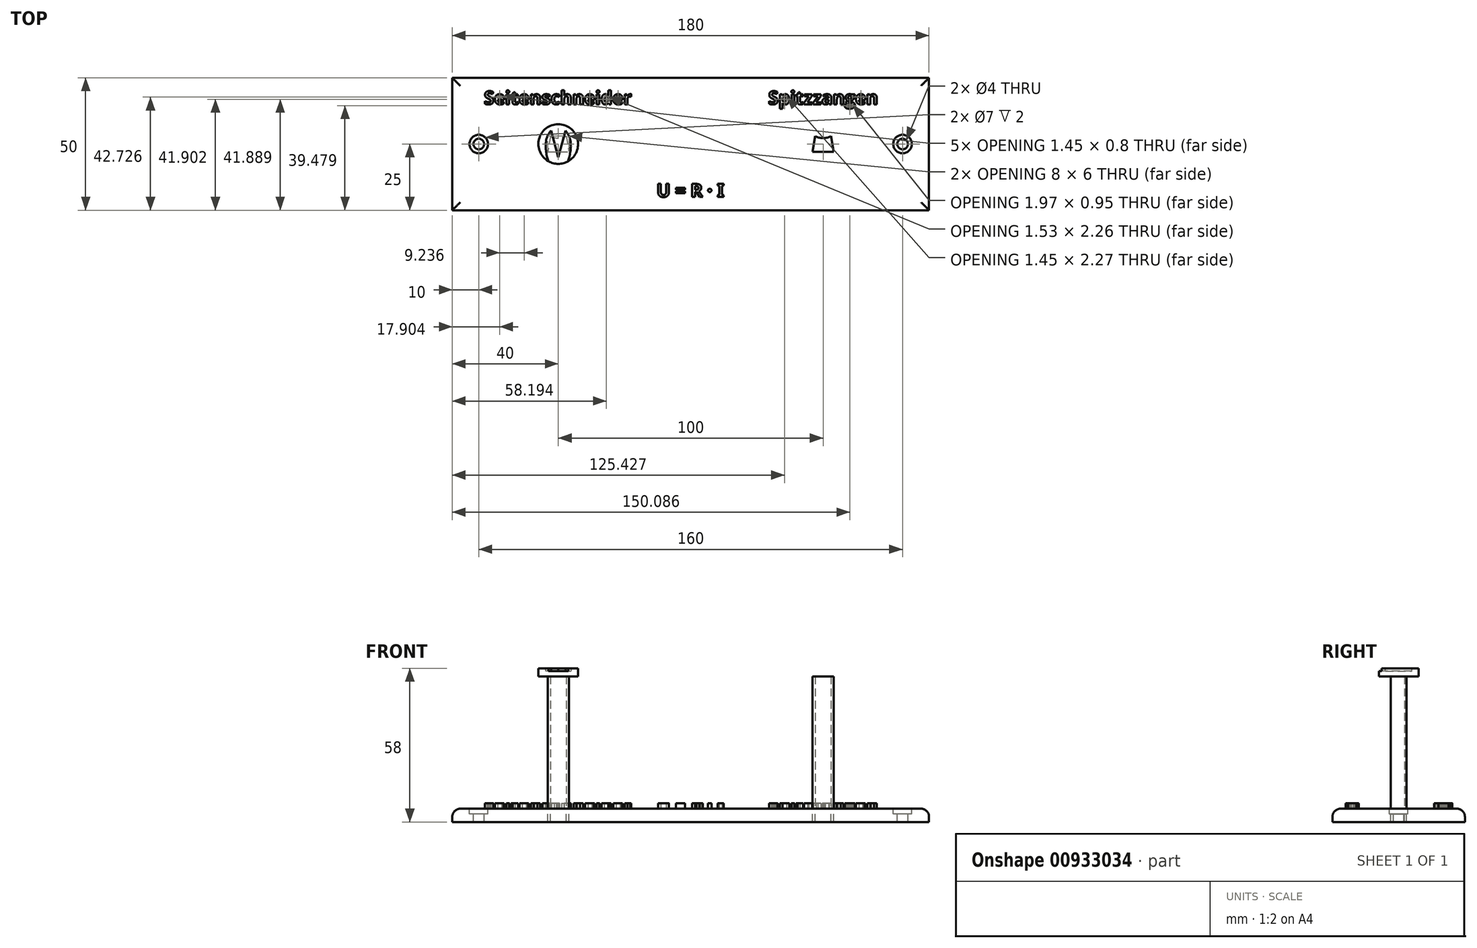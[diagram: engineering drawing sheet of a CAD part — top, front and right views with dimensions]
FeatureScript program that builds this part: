
annotation { "Feature Type Name" : "Feature", "Feature Type Description" : "" }
export const myFeature = defineFeature(function(context is Context, id is Id, definition is map)
    precondition{}
    {
        {
            var Q0;
            Q0=qCreatedBy(makeId("Top.planeOp"),FACE);
            var sketch = newSketch(context, id + "F0", { "sketchPlane" : qUnion([Q0])});
            skLineSegment(sketch, "E0.bottom", {"start": v(-90, 25) * mm, "end": v(90, 25) * mm});
            skLineSegment(sketch, "E0.top", {"start": v(-90, -25) * mm, "end": v(90, -25) * mm});
            skLineSegment(sketch, "E0.left", {"start": v(-90, 25) * mm, "end": v(-90, -25) * mm});
            skLineSegment(sketch, "E0.right", {"start": v(90, 25) * mm, "end": v(90, -25) * mm});
            skPoint(sketch, "E0.middle", {"position": v(0, 0) * mm});
            skPoint(sketch, "E1", {"position": v(-50, 0) * mm});
            skLineSegment(sketch, "E2", {"start": v(0, 25) * mm, "end": v(0, -25) * mm, "construction": true});
            skLineSegment(sketch, "E3", {"start": v(-90, 0) * mm, "end": v(0, 0) * mm, "construction": true});
            skLineSegment(sketch, "E4", {"start": v(0, 0) * mm, "end": v(90, 0) * mm, "construction": true});
            skPoint(sketch, "E5", {"position": v(50, 0) * mm});
            skLineSegment(sketch, "E6", {"start": v(-50, 25) * mm, "end": v(-50, -25) * mm, "construction": true});
            skArc(sketch, "E7", {"start": v(-53, 3) * mm, "mid": v(-51.55, 2.44) * mm, "end": v(-50, 2.25) * mm});
            skLineSegment(sketch, "E8", {"start": v(-53, 3) * mm, "end": v(-53.5, 0) * mm});
            skLineSegment(sketch, "E9", {"start": v(-53.5, 0) * mm, "end": v(-54, -3) * mm});
            skLineSegment(sketch, "E10", {"start": v(-54, -3) * mm, "end": v(-50, -3) * mm});
            skLineSegment(sketch, "E11.MirrorCS", {"start": v(-46, -3) * mm, "end": v(-50, -3) * mm});
            skLineSegment(sketch, "E12.MirrorCS", {"start": v(-47, 3) * mm, "end": v(-46.5, 0) * mm});
            skLineSegment(sketch, "E13.MirrorCS", {"start": v(-46.5, 0) * mm, "end": v(-46, -3) * mm});
            skArc(sketch, "E14.MirrorCS", {"start": v(-47, 3) * mm, "mid": v(-48.45, 2.44) * mm, "end": v(-50, 2.25) * mm});
            skLineSegment(sketch, "E15.MirrorCS", {"start": v(47, 3) * mm, "end": v(46.5, 0) * mm});
            skLineSegment(sketch, "E16.MirrorCS", {"start": v(46.5, 0) * mm, "end": v(46, -3) * mm});
            skLineSegment(sketch, "E17.MirrorCS", {"start": v(54, -3) * mm, "end": v(50, -3) * mm});
            skLineSegment(sketch, "E18.MirrorCS", {"start": v(46, -3) * mm, "end": v(50, -3) * mm});
            skLineSegment(sketch, "E19.MirrorCS", {"start": v(53, 3) * mm, "end": v(53.5, 0) * mm});
            skLineSegment(sketch, "E20.MirrorCS", {"start": v(53.5, 0) * mm, "end": v(54, -3) * mm});
            skArc(sketch, "E21.MirrorCS", {"start": v(53, 3) * mm, "mid": v(51.55, 2.44) * mm, "end": v(50, 2.25) * mm});
            skArc(sketch, "E22.MirrorCS", {"start": v(47, 3) * mm, "mid": v(48.45, 2.44) * mm, "end": v(50, 2.25) * mm});
            skText(sketch, "E23", { "text": "Seitenschneider", "fontName": "OpenSans-Bold.ttf"});
            skText(sketch, "E24", { "text": "Spitzzangen", "fontName": "OpenSans-Bold.ttf"});
            skLineSegment(sketch, "E25", {"start": v(50, 25) * mm, "end": v(50, -25) * mm, "construction": true});
            skText(sketch, "E26", { "text": "U = R   I", "fontName": "NotoSans-Bold.ttf"});
            skCircle(sketch, "E27", {"center": v(7.2, -17.5) * mm, "radius": 0.65 * mm});
            skPoint(sketch, "E27.centerSnap0", {"position": v(0, -17.5) * mm});
            skPoint(sketch, "E28", {"position": v(-80, 0) * mm});
            skPoint(sketch, "E29.MirrorP", {"position": v(80, 0) * mm});
            const initialGuessF0  = {"E23": [-0.07803, 0.015, 1, 0, 0.005], "E24": [0.0293, 0.015, 1, 0, 0.005], "E26": [-0.01288, -0.02, 1, 0, 0.005]};
            skSetInitialGuess(sketch, initialGuessF0);
            skSolve(sketch);
        }
        {
            var Q0;
            Q0=makeQuery(id+"F0.imprint","IMPRINT",FACE,{"disambiguationData":[TD([[makeQuery(id+"F0.imprint","IMPRINT",EDGE,{"derivedFrom":sQuery(id+"F0.wireOp",EDGE,"E0.bottom")}),-1.0]])]});
            var Q1;
            Q1=makeQuery(id+"F0.imprint","IMPRINT",FACE,{"disambiguationData":[TD([[makeQuery(id+"F0.imprint","IMPRINT",EDGE,{"derivedFrom":sQuery(id+"F0.wireOp",EDGE,"E23.sketch_text.stroke-211")}),-1.0]])]});
            var Q2;
            Q2=makeQuery(id+"F0.imprint","IMPRINT",FACE,{"disambiguationData":[TD([[makeQuery(id+"F0.imprint","IMPRINT",EDGE,{"derivedFrom":sQuery(id+"F0.wireOp",EDGE,"E24.sketch_text.stroke-51")}),-1.0]])]});
            var Q3;
            Q3=makeQuery(id+"F0.imprint","IMPRINT",FACE,{"disambiguationData":[TD([[makeQuery(id+"F0.imprint","IMPRINT",EDGE,{"derivedFrom":sQuery(id+"F0.wireOp",EDGE,"E24.sketch_text.stroke-78")}),-1.0]])]});
            var Q4;
            Q4=makeQuery(id+"F0.imprint","IMPRINT",FACE,{"disambiguationData":[TD([[makeQuery(id+"F0.imprint","IMPRINT",EDGE,{"derivedFrom":sQuery(id+"F0.wireOp",EDGE,"E7")}),-1.0]])]});
            var Q5;
            Q5=makeQuery(id+"F0.imprint","IMPRINT",FACE,{"disambiguationData":[TD([[makeQuery(id+"F0.imprint","IMPRINT",EDGE,{"derivedFrom":sQuery(id+"F0.wireOp",EDGE,"E24.sketch_text.stroke-204")}),-1.0]])]});
            var Q6;
            Q6=makeQuery(id+"F0.imprint","IMPRINT",FACE,{"disambiguationData":[TD([[makeQuery(id+"F0.imprint","IMPRINT",EDGE,{"derivedFrom":sQuery(id+"F0.wireOp",EDGE,"E23.sketch_text.stroke-75")}),-1.0]])]});
            var Q7;
            Q7=makeQuery(id+"F0.imprint","IMPRINT",FACE,{"disambiguationData":[TD([[makeQuery(id+"F0.imprint","IMPRINT",EDGE,{"derivedFrom":sQuery(id+"F0.wireOp",EDGE,"E26.sketch_text.stroke-15")}),-1.0]])]});
            var Q8;
            Q8=makeQuery(id+"F0.imprint","IMPRINT",FACE,{"disambiguationData":[TD([[makeQuery(id+"F0.imprint","IMPRINT",EDGE,{"derivedFrom":sQuery(id+"F0.wireOp",EDGE,"E23.sketch_text.stroke-57")}),-1.0]])]});
            var Q9;
            Q9=makeQuery(id+"F0.imprint","IMPRINT",FACE,{"disambiguationData":[TD([[makeQuery(id+"F0.imprint","IMPRINT",EDGE,{"derivedFrom":sQuery(id+"F0.wireOp",EDGE,"E23.sketch_text.stroke-229")}),1.0]])]});
            var Q10;
            Q10=makeQuery(id+"F0.imprint","IMPRINT",FACE,{"disambiguationData":[TD([[makeQuery(id+"F0.imprint","IMPRINT",EDGE,{"derivedFrom":sQuery(id+"F0.wireOp",EDGE,"E23.sketch_text.stroke-169")}),-1.0]])]});
            var Q11;
            Q11=makeQuery(id+"F0.imprint","IMPRINT",FACE,{"disambiguationData":[TD([[makeQuery(id+"F0.imprint","IMPRINT",EDGE,{"derivedFrom":sQuery(id+"F0.wireOp",EDGE,"E26.sketch_text.stroke-42")}),-1.0]])]});
            var Q12;
            Q12=makeQuery(id+"F0.imprint","IMPRINT",FACE,{"disambiguationData":[TD([[makeQuery(id+"F0.imprint","IMPRINT",EDGE,{"derivedFrom":sQuery(id+"F0.wireOp",EDGE,"E23.sketch_text.stroke-238")}),-1.0]])]});
            var Q13;
            Q13=makeQuery(id+"F0.imprint","IMPRINT",FACE,{"disambiguationData":[TD([[makeQuery(id+"F0.imprint","IMPRINT",EDGE,{"derivedFrom":sQuery(id+"F0.wireOp",EDGE,"E23.sketch_text.stroke-0")}),-1.0]])]});
            var Q14;
            Q14=makeQuery(id+"F0.imprint","IMPRINT",FACE,{"disambiguationData":[TD([[makeQuery(id+"F0.imprint","IMPRINT",EDGE,{"derivedFrom":sQuery(id+"F0.wireOp",EDGE,"E23.sketch_text.stroke-215")}),-1.0]])]});
            var Q15;
            Q15=makeQuery(id+"F0.imprint","IMPRINT",FACE,{"disambiguationData":[TD([[makeQuery(id+"F0.imprint","IMPRINT",EDGE,{"derivedFrom":sQuery(id+"F0.wireOp",EDGE,"E26.sketch_text.stroke-0")}),-1.0]])]});
            var Q16;
            Q16=makeQuery(id+"F0.imprint","IMPRINT",FACE,{"disambiguationData":[TD([[makeQuery(id+"F0.imprint","IMPRINT",EDGE,{"derivedFrom":sQuery(id+"F0.wireOp",EDGE,"E24.sketch_text.stroke-140")}),-1.0]])]});
            var Q17;
            Q17=makeQuery(id+"F0.imprint","IMPRINT",FACE,{"disambiguationData":[TD([[makeQuery(id+"F0.imprint","IMPRINT",EDGE,{"derivedFrom":sQuery(id+"F0.wireOp",EDGE,"E24.sketch_text.stroke-123")}),-1.0]])]});
            var Q18;
            Q18=makeQuery(id+"F0.imprint","IMPRINT",FACE,{"disambiguationData":[TD([[makeQuery(id+"F0.imprint","IMPRINT",EDGE,{"derivedFrom":sQuery(id+"F0.wireOp",EDGE,"E23.sketch_text.stroke-138")}),-1.0]])]});
            var Q19;
            Q19=makeQuery(id+"F0.imprint","IMPRINT",FACE,{"disambiguationData":[TD([[makeQuery(id+"F0.imprint","IMPRINT",EDGE,{"derivedFrom":sQuery(id+"F0.wireOp",EDGE,"E24.sketch_text.stroke-60")}),-1.0]])]});
            var Q20;
            Q20=makeQuery(id+"F0.imprint","IMPRINT",FACE,{"disambiguationData":[TD([[makeQuery(id+"F0.imprint","IMPRINT",EDGE,{"derivedFrom":sQuery(id+"F0.wireOp",EDGE,"E24.sketch_text.stroke-0")}),-1.0]])]});
            var Q21;
            Q21=makeQuery(id+"F0.imprint","IMPRINT",FACE,{"disambiguationData":[TD([[makeQuery(id+"F0.imprint","IMPRINT",EDGE,{"derivedFrom":sQuery(id+"F0.wireOp",EDGE,"E23.sketch_text.stroke-95")}),-1.0]])]});
            var Q22;
            Q22=makeQuery(id+"F0.imprint","IMPRINT",FACE,{"disambiguationData":[TD([[makeQuery(id+"F0.imprint","IMPRINT",EDGE,{"derivedFrom":sQuery(id+"F0.wireOp",EDGE,"E23.sketch_text.stroke-28")}),-1.0]])]});
            var Q23;
            Q23=makeQuery(id+"F0.imprint","IMPRINT",FACE,{"disambiguationData":[TD([[makeQuery(id+"F0.imprint","IMPRINT",EDGE,{"derivedFrom":sQuery(id+"F0.wireOp",EDGE,"E23.sketch_text.stroke-152")}),-1.0]])]});
            var Q24;
            Q24=makeQuery(id+"F0.imprint","IMPRINT",FACE,{"disambiguationData":[TD([[makeQuery(id+"F0.imprint","IMPRINT",EDGE,{"derivedFrom":sQuery(id+"F0.wireOp",EDGE,"E15.MirrorCS")}),1.0]])]});
            var Q25;
            Q25=makeQuery(id+"F0.imprint","IMPRINT",FACE,{"disambiguationData":[TD([[makeQuery(id+"F0.imprint","IMPRINT",EDGE,{"derivedFrom":sQuery(id+"F0.wireOp",EDGE,"E24.sketch_text.stroke-88")}),-1.0]])]});
            var Q26;
            Q26=makeQuery(id+"F0.imprint","IMPRINT",FACE,{"disambiguationData":[TD([[makeQuery(id+"F0.imprint","IMPRINT",EDGE,{"derivedFrom":sQuery(id+"F0.wireOp",EDGE,"E23.sketch_text.stroke-112")}),-1.0]])]});
            var Q27;
            Q27=makeQuery(id+"F0.imprint","IMPRINT",FACE,{"disambiguationData":[TD([[makeQuery(id+"F0.imprint","IMPRINT",EDGE,{"derivedFrom":sQuery(id+"F0.wireOp",EDGE,"E26.sketch_text.stroke-23")}),-1.0]])]});
            var Q28;
            Q28=makeQuery(id+"F0.imprint","IMPRINT",FACE,{"disambiguationData":[TD([[makeQuery(id+"F0.imprint","IMPRINT",EDGE,{"derivedFrom":sQuery(id+"F0.wireOp",EDGE,"E26.sketch_text.stroke-19")}),-1.0]])]});
            var Q29;
            Q29=makeQuery(id+"F0.imprint","IMPRINT",FACE,{"disambiguationData":[TD([[makeQuery(id+"F0.imprint","IMPRINT",EDGE,{"derivedFrom":sQuery(id+"F0.wireOp",EDGE,"E23.sketch_text.stroke-186")}),-1.0]])]});
            var Q30;
            Q30=makeQuery(id+"F0.imprint","IMPRINT",FACE,{"disambiguationData":[TD([[makeQuery(id+"F0.imprint","IMPRINT",EDGE,{"derivedFrom":sQuery(id+"F0.wireOp",EDGE,"E24.sketch_text.stroke-98")}),-1.0]])]});
            var Q31;
            Q31=makeQuery(id+"F0.imprint","IMPRINT",FACE,{"disambiguationData":[TD([[makeQuery(id+"F0.imprint","IMPRINT",EDGE,{"derivedFrom":sQuery(id+"F0.wireOp",EDGE,"E24.sketch_text.stroke-28")}),-1.0]])]});
            var Q32;
            Q32=makeQuery(id+"F0.imprint","IMPRINT",FACE,{"disambiguationData":[TD([[makeQuery(id+"F0.imprint","IMPRINT",EDGE,{"derivedFrom":sQuery(id+"F0.wireOp",EDGE,"E24.sketch_text.stroke-184")}),-1.0]])]});
            var Q33;
            Q33=makeQuery(id+"F0.imprint","IMPRINT",FACE,{"disambiguationData":[TD([[makeQuery(id+"F0.imprint","IMPRINT",EDGE,{"derivedFrom":sQuery(id+"F0.wireOp",EDGE,"E23.sketch_text.stroke-258")}),-1.0]])]});
            var Q34;
            Q34=makeQuery(id+"F0.imprint","IMPRINT",FACE,{"disambiguationData":[TD([[makeQuery(id+"F0.imprint","IMPRINT",EDGE,{"derivedFrom":sQuery(id+"F0.wireOp",EDGE,"E23.sketch_text.stroke-53")}),-1.0]])]});
            var Q35;
            Q35=makeQuery(id+"F0.imprint","IMPRINT",FACE,{"disambiguationData":[TD([[makeQuery(id+"F0.imprint","IMPRINT",EDGE,{"derivedFrom":sQuery(id+"F0.wireOp",EDGE,"E24.sketch_text.stroke-56")}),-1.0]])]});
            var Q36;
            Q36=makeQuery(id+"F0.imprint","IMPRINT",FACE,{"disambiguationData":[TD([[makeQuery(id+"F0.imprint","IMPRINT",EDGE,{"derivedFrom":sQuery(id+"F0.wireOp",EDGE,"E24.sketch_text.stroke-178")}),1.0]])]});
            var Q37;
            Q37=makeQuery(id+"F0.imprint","IMPRINT",FACE,{"disambiguationData":[TD([[makeQuery(id+"F0.imprint","IMPRINT",EDGE,{"derivedFrom":sQuery(id+"F0.wireOp",EDGE,"E23.sketch_text.stroke-28")}),1.0]])]});
            var Q38;
            Q38=makeQuery(id+"F0.imprint","IMPRINT",FACE,{"disambiguationData":[TD([[makeQuery(id+"F0.imprint","IMPRINT",EDGE,{"derivedFrom":sQuery(id+"F0.wireOp",EDGE,"E23.sketch_text.stroke-48")}),-1.0]])]});
            var Q39;
            Q39=makeQuery(id+"F0.imprint","IMPRINT",FACE,{"disambiguationData":[TD([[makeQuery(id+"F0.imprint","IMPRINT",EDGE,{"derivedFrom":sQuery(id+"F0.wireOp",EDGE,"E24.sketch_text.stroke-116")}),1.0]])]});
            var Q40;
            Q40=makeQuery(id+"F0.imprint","IMPRINT",FACE,{"disambiguationData":[TD([[makeQuery(id+"F0.imprint","IMPRINT",EDGE,{"derivedFrom":sQuery(id+"F0.wireOp",EDGE,"E23.sketch_text.stroke-206")}),-1.0]])]});
            var Q41;
            Q41=makeQuery(id+"F0.imprint","IMPRINT",FACE,{"disambiguationData":[TD([[makeQuery(id+"F0.imprint","IMPRINT",EDGE,{"derivedFrom":sQuery(id+"F0.wireOp",EDGE,"E24.sketch_text.stroke-184")}),1.0]])]});
            var Q42;
            Q42=makeQuery(id+"F0.imprint","IMPRINT",FACE,{"disambiguationData":[TD([[makeQuery(id+"F0.imprint","IMPRINT",EDGE,{"derivedFrom":sQuery(id+"F0.wireOp",EDGE,"E27")}),1.0]])]});
            var Q43;
            Q43=makeQuery(id+"F0.imprint","IMPRINT",FACE,{"disambiguationData":[TD([[makeQuery(id+"F0.imprint","IMPRINT",EDGE,{"derivedFrom":sQuery(id+"F0.wireOp",EDGE,"E24.sketch_text.stroke-43")}),1.0]])]});
            var Q44;
            Q44=makeQuery(id+"F0.imprint","IMPRINT",FACE,{"disambiguationData":[TD([[makeQuery(id+"F0.imprint","IMPRINT",EDGE,{"derivedFrom":sQuery(id+"F0.wireOp",EDGE,"E23.sketch_text.stroke-238")}),1.0]])]});
            var Q45;
            Q45=makeQuery(id+"F0.imprint","IMPRINT",FACE,{"disambiguationData":[TD([[makeQuery(id+"F0.imprint","IMPRINT",EDGE,{"derivedFrom":sQuery(id+"F0.wireOp",EDGE,"E23.sketch_text.stroke-75")}),1.0]])]});
            var Q46;
            Q46=makeQuery(id+"F0.imprint","IMPRINT",FACE,{"disambiguationData":[TD([[makeQuery(id+"F0.imprint","IMPRINT",EDGE,{"derivedFrom":sQuery(id+"F0.wireOp",EDGE,"E23.sketch_text.stroke-186")}),1.0]])]});
            var Q47;
            Q47=makeQuery(id+"F0.imprint","IMPRINT",FACE,{"disambiguationData":[TD([[makeQuery(id+"F0.imprint","IMPRINT",EDGE,{"derivedFrom":sQuery(id+"F0.wireOp",EDGE,"E26.sketch_text.stroke-23")}),1.0]])]});
            var Q48;
            Q48=makeQuery(id+"F0.imprint","IMPRINT",FACE,{"disambiguationData":[TD([[makeQuery(id+"F0.imprint","IMPRINT",EDGE,{"derivedFrom":sQuery(id+"F0.wireOp",EDGE,"E24.sketch_text.stroke-169")}),1.0]])]});
            extrude(context, id + "F1", {"entities" : qUnion([Q0, Q1, Q2, Q3, Q4, Q5, Q6, Q7, Q8, Q9, Q10, Q11, Q12, Q13, Q14, Q15, Q16, Q17, Q18, Q19, Q20, Q21, Q22, Q23, Q24, Q25, Q26, Q27, Q28, Q29, Q30, Q31, Q32, Q33, Q34, Q35, Q36, Q37, Q38, Q39, Q40, Q41, Q42, Q43, Q44, Q45, Q46, Q47, Q48]), "oppositeDirection" : true, "depth" : 5 * mm, "offsetDistance" : 25 * mm});
        }
        {
            var Q0;
            Q0=makeQuery(id+"F1.opExtrude","CAP_EDGE",EDGE,{"disambiguationData":[OSD([sQuery(id+"F0.wireOp",EDGE,"E0.bottom")])],"isStart":true});
            var Q1;
            Q1=makeQuery(id+"F1.opExtrude","CAP_EDGE",EDGE,{"disambiguationData":[OSD([sQuery(id+"F0.wireOp",EDGE,"E0.left")])],"isStart":true});
            var Q2;
            Q2=makeQuery(id+"F1.opExtrude","CAP_EDGE",EDGE,{"disambiguationData":[OSD([sQuery(id+"F0.wireOp",EDGE,"E0.top")])],"isStart":true});
            var Q3;
            Q3=makeQuery(id+"F1.opExtrude","CAP_EDGE",EDGE,{"disambiguationData":[OSD([sQuery(id+"F0.wireOp",EDGE,"E0.right")])],"isStart":true});
            fillet(context, id + "F2", {"entities" : qUnion([Q0, Q1, Q2, Q3]), "radius" : 3 * mm, "tangentPropagation" : true, "allowEdgeOverflow" : false});
        }
        {
            var Q0;
            Q0=makeQuery(id+"F0.imprint","IMPRINT",FACE,{"disambiguationData":[TD([[makeQuery(id+"F0.imprint","IMPRINT",EDGE,{"derivedFrom":sQuery(id+"F0.wireOp",EDGE,"E7")}),-1.0]])]});
            var Q1;
            Q1=makeQuery(id+"F0.imprint","IMPRINT",FACE,{"disambiguationData":[TD([[makeQuery(id+"F0.imprint","IMPRINT",EDGE,{"derivedFrom":sQuery(id+"F0.wireOp",EDGE,"E15.MirrorCS")}),1.0]])]});
            extrude(context, id + "F3", {"entities" : qUnion([Q0, Q1]), "depth" : 50 * mm, "offsetDistance" : 25 * mm});
        }
        {
            var Q0;
            Q0=makeQuery(id+"F0.imprint","IMPRINT",FACE,{"disambiguationData":[TD([[makeQuery(id+"F0.imprint","IMPRINT",EDGE,{"derivedFrom":sQuery(id+"F0.wireOp",EDGE,"E15.MirrorCS")}),1.0]])]});
            var Q1;
            Q1=makeQuery(id+"F0.imprint","IMPRINT",FACE,{"disambiguationData":[TD([[makeQuery(id+"F0.imprint","IMPRINT",EDGE,{"derivedFrom":sQuery(id+"F0.wireOp",EDGE,"E7")}),-1.0]])]});
            extrude(context, id + "F4", {"entities" : qUnion([Q0, Q1]), "operationType" : NewBodyOperationType.REMOVE, "oppositeDirection" : true, "depth" : 5 * mm, "offsetDistance" : 25 * mm});
        }
        {
            var Q0;
            Q0=makeQuery(id+"F0.imprint","IMPRINT",FACE,{"disambiguationData":[TD([[makeQuery(id+"F0.imprint","IMPRINT",EDGE,{"derivedFrom":sQuery(id+"F0.wireOp",EDGE,"E23.sketch_text.stroke-0")}),-1.0]])]});
            var Q1;
            Q1=makeQuery(id+"F0.imprint","IMPRINT",FACE,{"disambiguationData":[TD([[makeQuery(id+"F0.imprint","IMPRINT",EDGE,{"derivedFrom":sQuery(id+"F0.wireOp",EDGE,"E23.sketch_text.stroke-53")}),-1.0]])]});
            var Q2;
            Q2=makeQuery(id+"F0.imprint","IMPRINT",FACE,{"disambiguationData":[TD([[makeQuery(id+"F0.imprint","IMPRINT",EDGE,{"derivedFrom":sQuery(id+"F0.wireOp",EDGE,"E23.sketch_text.stroke-48")}),-1.0]])]});
            var Q3;
            Q3=makeQuery(id+"F0.imprint","IMPRINT",FACE,{"disambiguationData":[TD([[makeQuery(id+"F0.imprint","IMPRINT",EDGE,{"derivedFrom":sQuery(id+"F0.wireOp",EDGE,"E23.sketch_text.stroke-57")}),-1.0]])]});
            var Q4;
            Q4=makeQuery(id+"F0.imprint","IMPRINT",FACE,{"disambiguationData":[TD([[makeQuery(id+"F0.imprint","IMPRINT",EDGE,{"derivedFrom":sQuery(id+"F0.wireOp",EDGE,"E23.sketch_text.stroke-28")}),-1.0]])]});
            var Q5;
            Q5=makeQuery(id+"F0.imprint","IMPRINT",FACE,{"disambiguationData":[TD([[makeQuery(id+"F0.imprint","IMPRINT",EDGE,{"derivedFrom":sQuery(id+"F0.wireOp",EDGE,"E23.sketch_text.stroke-75")}),-1.0]])]});
            var Q6;
            Q6=makeQuery(id+"F0.imprint","IMPRINT",FACE,{"disambiguationData":[TD([[makeQuery(id+"F0.imprint","IMPRINT",EDGE,{"derivedFrom":sQuery(id+"F0.wireOp",EDGE,"E23.sketch_text.stroke-95")}),-1.0]])]});
            var Q7;
            Q7=makeQuery(id+"F0.imprint","IMPRINT",FACE,{"disambiguationData":[TD([[makeQuery(id+"F0.imprint","IMPRINT",EDGE,{"derivedFrom":sQuery(id+"F0.wireOp",EDGE,"E23.sketch_text.stroke-112")}),-1.0]])]});
            var Q8;
            Q8=makeQuery(id+"F0.imprint","IMPRINT",FACE,{"disambiguationData":[TD([[makeQuery(id+"F0.imprint","IMPRINT",EDGE,{"derivedFrom":sQuery(id+"F0.wireOp",EDGE,"E23.sketch_text.stroke-138")}),-1.0]])]});
            var Q9;
            Q9=makeQuery(id+"F0.imprint","IMPRINT",FACE,{"disambiguationData":[TD([[makeQuery(id+"F0.imprint","IMPRINT",EDGE,{"derivedFrom":sQuery(id+"F0.wireOp",EDGE,"E23.sketch_text.stroke-152")}),-1.0]])]});
            var Q10;
            Q10=makeQuery(id+"F0.imprint","IMPRINT",FACE,{"disambiguationData":[TD([[makeQuery(id+"F0.imprint","IMPRINT",EDGE,{"derivedFrom":sQuery(id+"F0.wireOp",EDGE,"E23.sketch_text.stroke-169")}),-1.0]])]});
            var Q11;
            Q11=makeQuery(id+"F0.imprint","IMPRINT",FACE,{"disambiguationData":[TD([[makeQuery(id+"F0.imprint","IMPRINT",EDGE,{"derivedFrom":sQuery(id+"F0.wireOp",EDGE,"E23.sketch_text.stroke-186")}),-1.0]])]});
            var Q12;
            Q12=makeQuery(id+"F0.imprint","IMPRINT",FACE,{"disambiguationData":[TD([[makeQuery(id+"F0.imprint","IMPRINT",EDGE,{"derivedFrom":sQuery(id+"F0.wireOp",EDGE,"E23.sketch_text.stroke-211")}),-1.0]])]});
            var Q13;
            Q13=makeQuery(id+"F0.imprint","IMPRINT",FACE,{"disambiguationData":[TD([[makeQuery(id+"F0.imprint","IMPRINT",EDGE,{"derivedFrom":sQuery(id+"F0.wireOp",EDGE,"E23.sketch_text.stroke-206")}),-1.0]])]});
            var Q14;
            Q14=makeQuery(id+"F0.imprint","IMPRINT",FACE,{"disambiguationData":[TD([[makeQuery(id+"F0.imprint","IMPRINT",EDGE,{"derivedFrom":sQuery(id+"F0.wireOp",EDGE,"E23.sketch_text.stroke-215")}),-1.0]])]});
            var Q15;
            Q15=makeQuery(id+"F0.imprint","IMPRINT",FACE,{"disambiguationData":[TD([[makeQuery(id+"F0.imprint","IMPRINT",EDGE,{"derivedFrom":sQuery(id+"F0.wireOp",EDGE,"E23.sketch_text.stroke-238")}),-1.0]])]});
            var Q16;
            Q16=makeQuery(id+"F0.imprint","IMPRINT",FACE,{"disambiguationData":[TD([[makeQuery(id+"F0.imprint","IMPRINT",EDGE,{"derivedFrom":sQuery(id+"F0.wireOp",EDGE,"E23.sketch_text.stroke-258")}),-1.0]])]});
            var Q17;
            Q17=makeQuery(id+"F0.imprint","IMPRINT",FACE,{"disambiguationData":[TD([[makeQuery(id+"F0.imprint","IMPRINT",EDGE,{"derivedFrom":sQuery(id+"F0.wireOp",EDGE,"E24.sketch_text.stroke-0")}),-1.0]])]});
            var Q18;
            Q18=makeQuery(id+"F0.imprint","IMPRINT",FACE,{"disambiguationData":[TD([[makeQuery(id+"F0.imprint","IMPRINT",EDGE,{"derivedFrom":sQuery(id+"F0.wireOp",EDGE,"E24.sketch_text.stroke-28")}),-1.0]])]});
            var Q19;
            Q19=makeQuery(id+"F0.imprint","IMPRINT",FACE,{"disambiguationData":[TD([[makeQuery(id+"F0.imprint","IMPRINT",EDGE,{"derivedFrom":sQuery(id+"F0.wireOp",EDGE,"E24.sketch_text.stroke-56")}),-1.0]])]});
            var Q20;
            Q20=makeQuery(id+"F0.imprint","IMPRINT",FACE,{"disambiguationData":[TD([[makeQuery(id+"F0.imprint","IMPRINT",EDGE,{"derivedFrom":sQuery(id+"F0.wireOp",EDGE,"E24.sketch_text.stroke-51")}),-1.0]])]});
            var Q21;
            Q21=makeQuery(id+"F0.imprint","IMPRINT",FACE,{"disambiguationData":[TD([[makeQuery(id+"F0.imprint","IMPRINT",EDGE,{"derivedFrom":sQuery(id+"F0.wireOp",EDGE,"E24.sketch_text.stroke-60")}),-1.0]])]});
            var Q22;
            Q22=makeQuery(id+"F0.imprint","IMPRINT",FACE,{"disambiguationData":[TD([[makeQuery(id+"F0.imprint","IMPRINT",EDGE,{"derivedFrom":sQuery(id+"F0.wireOp",EDGE,"E24.sketch_text.stroke-78")}),-1.0]])]});
            var Q23;
            Q23=makeQuery(id+"F0.imprint","IMPRINT",FACE,{"disambiguationData":[TD([[makeQuery(id+"F0.imprint","IMPRINT",EDGE,{"derivedFrom":sQuery(id+"F0.wireOp",EDGE,"E24.sketch_text.stroke-88")}),-1.0]])]});
            var Q24;
            Q24=makeQuery(id+"F0.imprint","IMPRINT",FACE,{"disambiguationData":[TD([[makeQuery(id+"F0.imprint","IMPRINT",EDGE,{"derivedFrom":sQuery(id+"F0.wireOp",EDGE,"E24.sketch_text.stroke-98")}),-1.0]])]});
            var Q25;
            Q25=makeQuery(id+"F0.imprint","IMPRINT",FACE,{"disambiguationData":[TD([[makeQuery(id+"F0.imprint","IMPRINT",EDGE,{"derivedFrom":sQuery(id+"F0.wireOp",EDGE,"E24.sketch_text.stroke-123")}),-1.0]])]});
            var Q26;
            Q26=makeQuery(id+"F0.imprint","IMPRINT",FACE,{"disambiguationData":[TD([[makeQuery(id+"F0.imprint","IMPRINT",EDGE,{"derivedFrom":sQuery(id+"F0.wireOp",EDGE,"E24.sketch_text.stroke-140")}),-1.0]])]});
            var Q27;
            Q27=makeQuery(id+"F0.imprint","IMPRINT",FACE,{"disambiguationData":[TD([[makeQuery(id+"F0.imprint","IMPRINT",EDGE,{"derivedFrom":sQuery(id+"F0.wireOp",EDGE,"E24.sketch_text.stroke-184")}),-1.0]])]});
            var Q28;
            Q28=makeQuery(id+"F0.imprint","IMPRINT",FACE,{"disambiguationData":[TD([[makeQuery(id+"F0.imprint","IMPRINT",EDGE,{"derivedFrom":sQuery(id+"F0.wireOp",EDGE,"E24.sketch_text.stroke-204")}),-1.0]])]});
            var Q29;
            Q29=makeQuery(id+"F0.imprint","IMPRINT",FACE,{"disambiguationData":[TD([[makeQuery(id+"F0.imprint","IMPRINT",EDGE,{"derivedFrom":sQuery(id+"F0.wireOp",EDGE,"E26.sketch_text.stroke-0")}),-1.0]])]});
            var Q30;
            Q30=makeQuery(id+"F0.imprint","IMPRINT",FACE,{"disambiguationData":[TD([[makeQuery(id+"F0.imprint","IMPRINT",EDGE,{"derivedFrom":sQuery(id+"F0.wireOp",EDGE,"E26.sketch_text.stroke-19")}),-1.0]])]});
            var Q31;
            Q31=makeQuery(id+"F0.imprint","IMPRINT",FACE,{"disambiguationData":[TD([[makeQuery(id+"F0.imprint","IMPRINT",EDGE,{"derivedFrom":sQuery(id+"F0.wireOp",EDGE,"E26.sketch_text.stroke-15")}),-1.0]])]});
            var Q32;
            Q32=makeQuery(id+"F0.imprint","IMPRINT",FACE,{"disambiguationData":[TD([[makeQuery(id+"F0.imprint","IMPRINT",EDGE,{"derivedFrom":sQuery(id+"F0.wireOp",EDGE,"E26.sketch_text.stroke-23")}),-1.0]])]});
            var Q33;
            Q33=makeQuery(id+"F0.imprint","IMPRINT",FACE,{"disambiguationData":[TD([[makeQuery(id+"F0.imprint","IMPRINT",EDGE,{"derivedFrom":sQuery(id+"F0.wireOp",EDGE,"E27")}),1.0]])]});
            var Q34;
            Q34=makeQuery(id+"F0.imprint","IMPRINT",FACE,{"disambiguationData":[TD([[makeQuery(id+"F0.imprint","IMPRINT",EDGE,{"derivedFrom":sQuery(id+"F0.wireOp",EDGE,"E26.sketch_text.stroke-42")}),-1.0]])]});
            extrude(context, id + "F5", {"entities" : qUnion([Q0, Q1, Q2, Q3, Q4, Q5, Q6, Q7, Q8, Q9, Q10, Q11, Q12, Q13, Q14, Q15, Q16, Q17, Q18, Q19, Q20, Q21, Q22, Q23, Q24, Q25, Q26, Q27, Q28, Q29, Q30, Q31, Q32, Q33, Q34]), "depth" : 2 * mm, "offsetDistance" : 25 * mm});
        }
        {
            var Q0;
            Q0=sQuery(id+"F0.wireOp",VERTEX,"E28");
            var Q1;
            Q1=sQuery(id+"F0.wireOp",VERTEX,"E29.MirrorP");
            var Q2;
            Q2=makeQuery(id+"F1.opExtrude","SWEPT_BODY",BODY,{"disambiguationData":[OSD([sQuery(id+"F0.wireOp",EDGE,"E0.bottom"),sQuery(id+"F0.wireOp",EDGE,"E0.top"),sQuery(id+"F0.wireOp",EDGE,"E0.left"),sQuery(id+"F0.wireOp",EDGE,"E0.right")])]});
            hole(context, id + "F6", {"style" : HoleStyle.C_BORE, "endStyle" : HoleEndStyle.THROUGH, "holeDiameter" : 4 * mm, "cBoreDiameter" : 7 * mm, "cBoreDepth" : 2 * mm, "majorDiameter" : 5 * mm, "isTappedThrough" : true, "tappedDepth" : 12 * mm, "tapClearance" : 3, "locations" : qUnion([Q0, Q1]), "scope" : qUnion([Q2])});
        }
        {
            var Q0;
            Q0=makeQuery(id+"F3.opExtrude","CAP_FACE",FACE,{"disambiguationData":[OSD([sQuery(id+"F0.wireOp",EDGE,"E7"),sQuery(id+"F0.wireOp",EDGE,"E8"),sQuery(id+"F0.wireOp",EDGE,"E9"),sQuery(id+"F0.wireOp",EDGE,"E10"),sQuery(id+"F0.wireOp",EDGE,"E11.MirrorCS"),sQuery(id+"F0.wireOp",EDGE,"E12.MirrorCS"),sQuery(id+"F0.wireOp",EDGE,"E13.MirrorCS"),sQuery(id+"F0.wireOp",EDGE,"E14.MirrorCS")])],"isStart":false});
            var sketch = newSketch(context, id + "F7", { "sketchPlane" : qUnion([Q0])});
            skCircle(sketch, "E30", {"center": v(-50, 0) * mm, "radius": 7.5 * mm});
            skCircle(sketch, "E31.MirrorC", {"center": v(50, 0) * mm, "radius": 7.5 * mm});
            skSolve(sketch);
        }
        {
            var Q0;
            Q0=makeQuery(id+"F7.imprint","IMPRINT",FACE,{"disambiguationData":[TD([[makeQuery(id+"F7.imprint","IMPRINT",EDGE,{"derivedFrom":sQuery(id+"F7.wireOp",EDGE,"E31.MirrorC")}),-1.0]])]});
            var Q1;
            {var subQ1=sQuery(id+"F7.wireOp",EDGE,"frd1I7if-Ppwl-jtBj-eDqs-HEHFfIM9dH6L");var subQ3=makeQuery(id+"F3.opExtrude","CAP_EDGE",EDGE,{"disambiguationData":[OSD([sQuery(id+"F0.wireOp",EDGE,"E10"),sQuery(id+"F0.wireOp",EDGE,"E11.MirrorCS")])],"isStart":false});var subQ4=makeQuery(id+"F7.imprint","INTERSECT",VERTEX,{"derivedFrom":[subQ3,subQ1]});Q1=makeQuery(id+"F7.imprint","IMPRINT",FACE,{"disambiguationData":[TD([[makeQuery(id+"F7.imprint","IMPRINT",EDGE,{"disambiguationData":[TD([[subQ4,1.0]])],"derivedFrom":subQ1}),1.0]])]});}
            var Q2;
            {var subQ0=sQuery(id+"F7.wireOp",EDGE,"frd1I7if-Ppwl-jtBj-eDqs-HEHFfIM9dH6L");var subQ1=makeQuery(id+"F3.opExtrude","CAP_EDGE",EDGE,{"disambiguationData":[OSD([sQuery(id+"F0.wireOp",EDGE,"E10"),sQuery(id+"F0.wireOp",EDGE,"E11.MirrorCS")])],"isStart":false});var subQ2=makeQuery(id+"F7.imprint","INTERSECT",VERTEX,{"derivedFrom":[subQ1,subQ0]});Q2=makeQuery(id+"F7.imprint","IMPRINT",FACE,{"disambiguationData":[TD([[makeQuery(id+"F7.imprint","IMPRINT",EDGE,{"disambiguationData":[TD([[subQ2,-1.0]])],"derivedFrom":subQ0}),1.0]])]});}
            var Q3;
            Q3=makeQuery(id+"F7.imprint","IMPRINT",FACE,{"disambiguationData":[TD([[makeQuery(id+"F7.imprint","IMPRINT",EDGE,{"derivedFrom":sQuery(id+"F7.wireOp",EDGE,"E30")}),1.0]])]});
            var Q4;
            {var subQ4=sQuery(id+"F7.wireOp",EDGE,"fc13d614-929a-4f41-b516-a1333a8aa3a70.MirrorCS");Q4=makeQuery(id+"F7.imprint","IMPRINT",FACE,{"disambiguationData":[TD([[makeQuery(id+"F7.imprint","IMPRINT",EDGE,{"derivedFrom":subQ4}),-1.0]])]});}
            var Q5;
            {var subQ1=sQuery(id+"F7.wireOp",EDGE,"eVV4xVaZ-gbMO-8Qpw-5Zgi-2TiLExErDRlw");Q5=makeQuery(id+"F7.imprint","IMPRINT",FACE,{"disambiguationData":[TD([[makeQuery(id+"F7.imprint","IMPRINT",EDGE,{"derivedFrom":subQ1}),1.0]])]});}
            var Q6;
            {var subQ5=makeQuery(id+"F3.opExtrude","CAP_EDGE",EDGE,{"disambiguationData":[OSD([sQuery(id+"F0.wireOp",EDGE,"E8"),sQuery(id+"F0.wireOp",EDGE,"E9")])],"isStart":false});Q6=makeQuery(id+"F7.imprint","IMPRINT",FACE,{"disambiguationData":[TD([[makeQuery(id+"F7.imprint","IMPRINT",EDGE,{"derivedFrom":subQ5}),1.0]])]});}
            var Q7;
            {var subQ5=makeQuery(id+"F3.opExtrude","CAP_EDGE",EDGE,{"disambiguationData":[OSD([sQuery(id+"F0.wireOp",EDGE,"E12.MirrorCS"),sQuery(id+"F0.wireOp",EDGE,"E13.MirrorCS")])],"isStart":false});Q7=makeQuery(id+"F7.imprint","IMPRINT",FACE,{"disambiguationData":[TD([[makeQuery(id+"F7.imprint","IMPRINT",EDGE,{"derivedFrom":subQ5}),-1.0]])]});}
            extrude(context, id + "F8", {"entities" : qUnion([Q0, Q1, Q2, Q3, Q4, Q5, Q6, Q7]), "operationType" : NewBodyOperationType.ADD, "depth" : 3 * mm, "offsetDistance" : 25 * mm});
        }
        {
            var Q0;
            Q0=makeQuery(id+"F8.opExtrude","CAP_FACE",FACE,{"disambiguationData":[OSD([sQuery(id+"F7.wireOp",EDGE,"E30")])],"isStart":false});
            var sketch = newSketch(context, id + "F9", { "sketchPlane" : qUnion([Q0])});
            skLineSegment(sketch, "E32", {"start": v(-50, 7.5) * mm, "end": v(-50, -7.5) * mm, "construction": true});
            skLineSegment(sketch, "E33", {"start": v(-50, -5) * mm, "end": v(-47.27, 5) * mm});
            skFitSpline(sketch, "E34", {"points": [v(-47.27, 5) * mm, v(-46.26, -6.5) * mm], "startDerivative": vector(9.72, -9.91) * mm, "endDerivative": vector(-2.34, -7.49) * mm});
            skPoint(sketch, "E35", {"position": v(-50, 0) * mm});
            skFitSpline(sketch, "E36.MirrorCS", {"points": [v(-52.73, 5) * mm, v(-53.74, -6.5) * mm], "startDerivative": vector(-9.72, -9.91) * mm, "endDerivative": vector(2.34, -7.49) * mm});
            skLineSegment(sketch, "E37.MirrorCS", {"start": v(-50, -5) * mm, "end": v(-52.73, 5) * mm});
            skLineSegment(sketch, "E38", {"start": v(-42.5, 0) * mm, "end": v(-57.5, 0) * mm, "construction": true});
            skSolve(sketch);
        }
        {
            var Q0;
            Q0=makeQuery(id+"F8.opExtrude","CAP_FACE",FACE,{"disambiguationData":[OSD([sQuery(id+"F7.wireOp",EDGE,"E31.MirrorC")])],"isStart":false});
            var sketch = newSketch(context, id + "F10", { "sketchPlane" : qUnion([Q0])});
            skPoint(sketch, "E39", {"position": v(50, 0) * mm});
            skLineSegment(sketch, "E40", {"start": v(50, 7.5) * mm, "end": v(50, -7.5) * mm, "construction": true});
            skLineSegment(sketch, "E41", {"start": v(42.5, 0) * mm, "end": v(57.5, 0) * mm, "construction": true});
            skLineSegment(sketch, "E42", {"start": v(50, -10) * mm, "end": v(54, 5) * mm});
            skLineSegment(sketch, "E43", {"start": v(53.5, -6.63) * mm, "end": v(54.5, 4.05) * mm});
            skFitSpline(sketch, "E44", {"points": [v(54, 5) * mm, v(54.5, 4.05) * mm], "startDerivative": vector(1.35, -0.33) * mm, "endDerivative": vector(-0.03, -0.9) * mm});
            skFitSpline(sketch, "E45.MirrorCS", {"points": [v(46, 5) * mm, v(45.5, 4.05) * mm], "startDerivative": vector(-1.35, -0.33) * mm, "endDerivative": vector(0.03, -0.9) * mm});
            skLineSegment(sketch, "E46.MirrorCS", {"start": v(46.5, -6.63) * mm, "end": v(45.5, 4.05) * mm});
            skLineSegment(sketch, "E47.MirrorCS", {"start": v(50, -10) * mm, "end": v(46, 5) * mm});
            skSolve(sketch);
        }
        {
            var Q0;
            Q0=makeQuery(id+"F9.imprint","IMPRINT",FACE,{"disambiguationData":[TD([[makeQuery(id+"F9.imprint","IMPRINT",EDGE,{"derivedFrom":sQuery(id+"F9.wireOp",EDGE,"E33")}),-1.0]])]});
            var Q1;
            Q1=makeQuery(id+"F10.imprint","IMPRINT",FACE,{"disambiguationData":[TD([[makeQuery(id+"F10.imprint","IMPRINT",EDGE,{"derivedFrom":sQuery(id+"F10.wireOp",EDGE,"E42")}),-1.0]])]});
            var Q2;
            {var subQ0=sQuery(id+"F10.wireOp",EDGE,"E45.MirrorCS");Q2=makeQuery(id+"F10.imprint","IMPRINT",FACE,{"disambiguationData":[TD([[makeQuery(id+"F10.imprint","IMPRINT",EDGE,{"derivedFrom":subQ0}),1.0]])]});}
            extrude(context, id + "F11", {"entities" : qUnion([Q0, Q1, Q2]), "operationType" : NewBodyOperationType.REMOVE, "oppositeDirection" : true, "depth" : 1 * mm, "offsetDistance" : 25 * mm});
        }
    });
